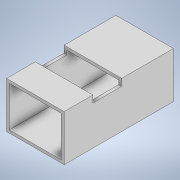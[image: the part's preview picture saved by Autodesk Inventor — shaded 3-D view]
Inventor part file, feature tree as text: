
AUTODESK INVENTOR PART (.ipt)
format: ipt  version: 2020 (Build 240168000, 168)  size: 134,144 bytes
history: native  units: in
note: dims shown in document units (in); Inventor stores cm internally (conversion verified against a paired STEP export)
features: extrude x4, sketch x4, projected_geometry x3
ambient origin geometry x8: Origin, YZ Plane, XZ Plane, XY Plane, X Axis, Y Axis, Z Axis, Center Point
bodies: Solid1 (feature_tree)
feature tree (11):
  extrude  "Extrusion1"  Depth=3.7402in
  extrude  "Extrusion2"  Depth=0.0984in
  extrude  "Extrusion3"  Depth=1.378in
  extrude  "Extrusion4"  Depth=1.7717in
  sketch  "Sketch1"  dims[d0=1.9685in d1=3.7402in]
  sketch  "Sketch2"  dims[d2=1.5748in d3=0.0in d4=0.0984in]
  projected_geometry  "Projected Loop1"
  sketch  "Sketch3"  dims[d5=1.7717in d6=1.378in]
  projected_geometry  "Projected Loop2"
  sketch  "Sketch4"  dims[d7=3.5433in d8=0.0in d9=1.7717in d10=2.7559in d11=0.2362in d12=0.0in d13=0.9843in d14=0.2362in d15=0.0in]
  projected_geometry  "Projected Loop3"
